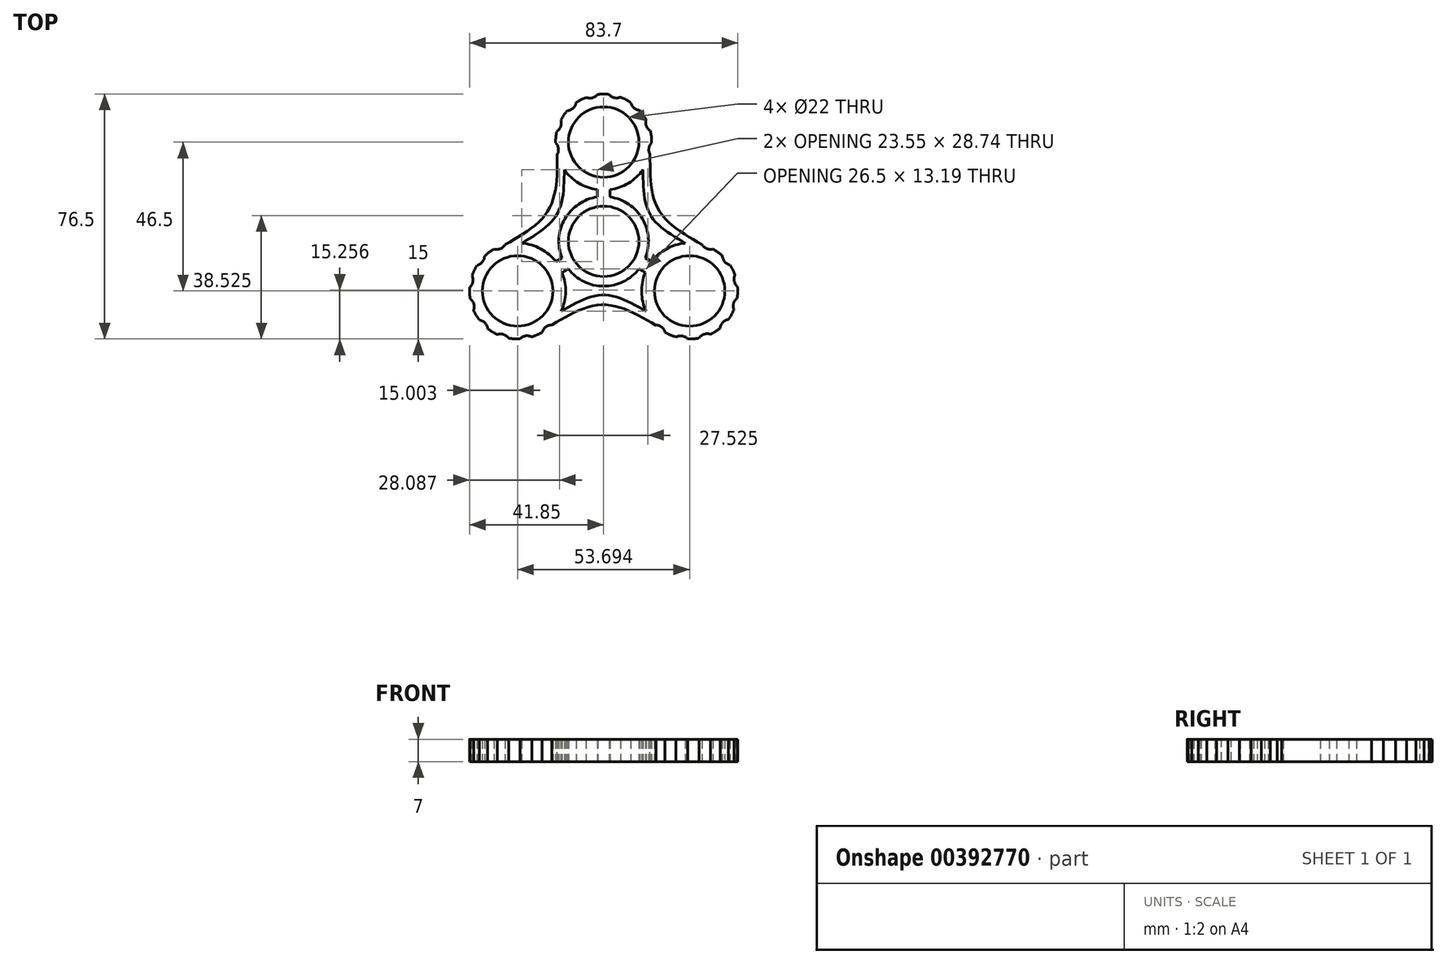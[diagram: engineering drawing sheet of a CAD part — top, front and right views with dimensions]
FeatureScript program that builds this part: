
annotation { "Feature Type Name" : "Feature", "Feature Type Description" : "" }
export const myFeature = defineFeature(function(context is Context, id is Id, definition is map)
    precondition{}
    {
        {
            var Q0;
            Q0=qCreatedBy(makeId("Top.planeOp"),FACE);
            var sketch = newSketch(context, id + "F0", { "sketchPlane" : qUnion([Q0])});
            skCircle(sketch, "E0", {"center": v(0, 0) * mm, "radius": 11 * mm});
            skCircle(sketch, "E1", {"center": v(0, 31) * mm, "radius": 11 * mm});
            skCircle(sketch, "E2.0", {"center": v(0, 0) * mm, "radius": 14 * mm});
            skArc(sketch, "E3.0", {"start": v(-14.49, 27.12) * mm, "mid": v(0.1, 16) * mm, "end": v(14.54, 27.3) * mm});
            skLineSegment(sketch, "E4", {"start": v(-1.99, 16.13) * mm, "end": v(-1.99, 13.86) * mm});
            skLineSegment(sketch, "E5.MirrorCS", {"start": v(1.99, 16.13) * mm, "end": v(1.99, 13.86) * mm});
            skLineSegment(sketch, "E6", {"start": v(0, 0) * mm, "end": v(-12.12, 7) * mm});
            skLineSegment(sketch, "E7", {"start": v(0, 31) * mm, "end": v(-14.49, 27.12) * mm, "construction": true});
            skLineSegment(sketch, "E8.MirrorCS", {"start": v(0, 31) * mm, "end": v(14.49, 27.12) * mm, "construction": true});
            skLineSegment(sketch, "E9", {"start": v(0, 31) * mm, "end": v(-12.29, 22.4) * mm, "construction": true});
            skLineSegment(sketch, "E10.MirrorCS", {"start": v(0, 31) * mm, "end": v(12.29, 22.4) * mm, "construction": true});
            skPoint(sketch, "E11.center", {"position": v(-1.16, -1.95) * mm});
            skPoint(sketch, "E12", {"position": v(-14.5, 8.41) * mm});
            skPoint(sketch, "E13.2.1", {"position": v(14.62, 8.4) * mm});
            skPoint(sketch, "E14.center", {"position": v(0, 0.05) * mm});
            skPoint(sketch, "E15", {"position": v(-17.14, 9.94) * mm});
            skPoint(sketch, "E16.MirrorP", {"position": v(17.14, 9.94) * mm});
            skArc(sketch, "E17", {"start": v(-14.49, 27.12) * mm, "mid": v(-14.12, 29.05) * mm, "end": v(-15, 30.8) * mm});
            skArc(sketch, "E18.MirrorCS", {"start": v(14.49, 27.12) * mm, "mid": v(14.12, 29.05) * mm, "end": v(15, 30.8) * mm});
            skPoint(sketch, "E19", {"position": v(14.49, 27.12) * mm});
            skPoint(sketch, "E20", {"position": v(15, 30.8) * mm});
            skArc(sketch, "E21.1.0", {"start": v(-14.62, 34.34) * mm, "mid": v(-13.4, 35.87) * mm, "end": v(-13.35, 37.83) * mm});
            skArc(sketch, "E21.2.0", {"start": v(-11.37, 40.78) * mm, "mid": v(-9.57, 41.56) * mm, "end": v(-8.61, 43.28) * mm});
            skArc(sketch, "E21.3.0", {"start": v(-5.48, 44.96) * mm, "mid": v(-3.52, 44.8) * mm, "end": v(-1.88, 45.88) * mm});
            skArc(sketch, "E21.4.0", {"start": v(1.68, 45.9) * mm, "mid": v(3.34, 44.85) * mm, "end": v(5.3, 45.03) * mm});
            skArc(sketch, "E21.5.0", {"start": v(8.45, 43.4) * mm, "mid": v(9.43, 41.69) * mm, "end": v(11.24, 40.93) * mm});
            skArc(sketch, "E21.6.0", {"start": v(13.26, 38) * mm, "mid": v(13.33, 36.05) * mm, "end": v(14.58, 34.53) * mm});
            skArc(sketch, "E21.7.0", {"start": v(14.14, 29.23) * mm, "mid": v(14.18, 28.24) * mm, "end": v(14.54, 27.3) * mm});
            skLineSegment(sketch, "E21.anchor1", {"start": v(0, 31) * mm, "end": v(-17.13, 28.63) * mm, "construction": true});
            skLineSegment(sketch, "E21.anchor2", {"start": v(0, 31) * mm, "end": v(17.16, 28.86) * mm, "construction": true});
            skArc(sketch, "E22.trimOffspring", {"start": v(-14.62, 34.34) * mm, "mid": v(-14.92, 32.58) * mm, "end": v(-15, 30.8) * mm});
            skArc(sketch, "E23.trimOffspring", {"start": v(-11.37, 40.78) * mm, "mid": v(-12.45, 39.37) * mm, "end": v(-13.35, 37.83) * mm});
            skArc(sketch, "E24.trimOffspring", {"start": v(-5.48, 44.96) * mm, "mid": v(-7.1, 44.22) * mm, "end": v(-8.61, 43.28) * mm});
            skArc(sketch, "E25.trimOffspring", {"start": v(1.68, 45.9) * mm, "mid": v(-0.1, 46) * mm, "end": v(-1.88, 45.88) * mm});
            skArc(sketch, "E26.trimOffspring", {"start": v(8.45, 43.4) * mm, "mid": v(6.92, 44.3) * mm, "end": v(5.3, 45.03) * mm});
            skArc(sketch, "E27.trimOffspring", {"start": v(13.26, 38) * mm, "mid": v(12.34, 39.53) * mm, "end": v(11.24, 40.93) * mm});
            skArc(sketch, "E28.trimOffspring", {"start": v(15, 30.8) * mm, "mid": v(14.9, 32.68) * mm, "end": v(14.58, 34.53) * mm});
            skPoint(sketch, "E29.orphan", {"position": v(15, 31) * mm});
            skArc(sketch, "E30.1.0", {"start": v(-40.6, -21.5) * mm, "mid": v(-39.79, -23.09) * mm, "end": v(-38.8, -24.57) * mm});
            skArc(sketch, "E30.1.1", {"start": v(-40.6, -21.5) * mm, "mid": v(-40.51, -19.54) * mm, "end": v(-41.65, -17.93) * mm});
            skArc(sketch, "E30.1.2", {"start": v(-41.8, -14.38) * mm, "mid": v(-41.83, -16.16) * mm, "end": v(-41.65, -17.93) * mm});
            skArc(sketch, "E30.1.3", {"start": v(-41.8, -14.38) * mm, "mid": v(-40.82, -12.68) * mm, "end": v(-41.07, -10.73) * mm});
            skArc(sketch, "E30.1.4", {"start": v(-39.55, -7.52) * mm, "mid": v(-40.4, -9.08) * mm, "end": v(-41.07, -10.73) * mm});
            skArc(sketch, "E30.1.5", {"start": v(-39.55, -7.52) * mm, "mid": v(-37.88, -6.48) * mm, "end": v(-37.2, -4.64) * mm});
            skPoint(sketch, "E30.1.6", {"position": v(-34.17, -2.41) * mm});
            skArc(sketch, "E30.1.7", {"start": v(-30.73, -1.01) * mm, "mid": v(-32.21, -2.3) * mm, "end": v(-34.17, -2.41) * mm});
            skArc(sketch, "E30.1.8", {"start": v(-34.17, -2.41) * mm, "mid": v(-35.75, -3.43) * mm, "end": v(-37.2, -4.64) * mm});
            skArc(sketch, "E30.1.9", {"start": v(-16.24, -26.1) * mm, "mid": v(-13.9, -7.91) * mm, "end": v(-30.92, -1.06) * mm});
            skArc(sketch, "E30.1.10", {"start": v(-16.24, -26.1) * mm, "mid": v(-18.1, -26.75) * mm, "end": v(-19.18, -28.4) * mm});
            skArc(sketch, "E30.1.11", {"start": v(-22.43, -29.83) * mm, "mid": v(-20.76, -29.2) * mm, "end": v(-19.18, -28.4) * mm});
            skArc(sketch, "E30.1.12", {"start": v(-22.43, -29.83) * mm, "mid": v(-24.37, -29.53) * mm, "end": v(-26.09, -30.48) * mm});
            skArc(sketch, "E30.1.13", {"start": v(-29.64, -30.24) * mm, "mid": v(-27.87, -30.47) * mm, "end": v(-26.09, -30.48) * mm});
            skArc(sketch, "E30.1.14", {"start": v(-29.64, -30.24) * mm, "mid": v(-31.21, -29.07) * mm, "end": v(-33.18, -29.1) * mm});
            skArc(sketch, "E30.1.15", {"start": v(-36.2, -27.23) * mm, "mid": v(-34.74, -28.25) * mm, "end": v(-33.18, -29.1) * mm});
            skArc(sketch, "E30.1.16", {"start": v(-36.2, -27.23) * mm, "mid": v(-37.04, -25.45) * mm, "end": v(-38.8, -24.57) * mm});
            skCircle(sketch, "E30.1.17", {"center": v(-26.85, -15.5) * mm, "radius": 11 * mm});
            skLineSegment(sketch, "E30.1.18", {"start": v(-14.96, -6.35) * mm, "end": v(-13, -5.2) * mm});
            skLineSegment(sketch, "E30.1.19", {"start": v(-12.98, -9.79) * mm, "end": v(-11, -8.65) * mm});
            skPoint(sketch, "E30.1.20", {"position": v(-0.04, -19.8) * mm});
            skPoint(sketch, "E30.1.21", {"position": v(-0.04, -16.76) * mm});
            skPoint(sketch, "E30.1.22", {"position": v(-14.58, 8.46) * mm});
            skPoint(sketch, "E30.1.23", {"position": v(-17.17, 9.87) * mm});
            skArc(sketch, "E30.2.0", {"start": v(38.92, -24.4) * mm, "mid": v(39.89, -22.91) * mm, "end": v(40.67, -21.32) * mm});
            skArc(sketch, "E30.2.1", {"start": v(38.92, -24.4) * mm, "mid": v(37.18, -25.32) * mm, "end": v(36.35, -27.1) * mm});
            skArc(sketch, "E30.2.2", {"start": v(33.36, -29.01) * mm, "mid": v(34.91, -28.15) * mm, "end": v(36.35, -27.1) * mm});
            skArc(sketch, "E30.2.3", {"start": v(33.36, -29.01) * mm, "mid": v(31.4, -29) * mm, "end": v(29.83, -30.2) * mm});
            skArc(sketch, "E30.2.4", {"start": v(26.29, -30.49) * mm, "mid": v(28.07, -30.45) * mm, "end": v(29.83, -30.2) * mm});
            skArc(sketch, "E30.2.5", {"start": v(26.29, -30.49) * mm, "mid": v(24.55, -29.56) * mm, "end": v(22.62, -29.9) * mm});
            skPoint(sketch, "E30.2.6", {"position": v(19.18, -28.4) * mm});
            skArc(sketch, "E30.2.7", {"start": v(16.24, -26.1) * mm, "mid": v(18.1, -26.75) * mm, "end": v(19.18, -28.4) * mm});
            skArc(sketch, "E30.2.8", {"start": v(19.18, -28.4) * mm, "mid": v(20.85, -29.25) * mm, "end": v(22.62, -29.9) * mm});
            skArc(sketch, "E30.2.9", {"start": v(30.73, -1.01) * mm, "mid": v(13.8, -8.09) * mm, "end": v(16.38, -26.25) * mm});
            skArc(sketch, "E30.2.10", {"start": v(30.73, -1.01) * mm, "mid": v(32.21, -2.3) * mm, "end": v(34.17, -2.41) * mm});
            skArc(sketch, "E30.2.11", {"start": v(37.05, -4.5) * mm, "mid": v(35.67, -3.37) * mm, "end": v(34.17, -2.41) * mm});
            skArc(sketch, "E30.2.12", {"start": v(37.05, -4.5) * mm, "mid": v(37.76, -6.34) * mm, "end": v(39.44, -7.35) * mm});
            skArc(sketch, "E30.2.13", {"start": v(41, -10.55) * mm, "mid": v(40.32, -8.9) * mm, "end": v(39.44, -7.35) * mm});
            skArc(sketch, "E30.2.14", {"start": v(41, -10.55) * mm, "mid": v(40.78, -12.5) * mm, "end": v(41.79, -14.18) * mm});
            skArc(sketch, "E30.2.15", {"start": v(41.68, -17.74) * mm, "mid": v(41.84, -15.96) * mm, "end": v(41.79, -14.18) * mm});
            skArc(sketch, "E30.2.16", {"start": v(41.68, -17.74) * mm, "mid": v(40.57, -19.35) * mm, "end": v(40.67, -21.32) * mm});
            skCircle(sketch, "E30.2.17", {"center": v(26.85, -15.5) * mm, "radius": 11 * mm});
            skLineSegment(sketch, "E30.2.18", {"start": v(12.98, -9.79) * mm, "end": v(11, -8.65) * mm});
            skLineSegment(sketch, "E30.2.19", {"start": v(14.96, -6.35) * mm, "end": v(13, -5.2) * mm});
            skPoint(sketch, "E30.2.20", {"position": v(17.17, 9.87) * mm});
            skPoint(sketch, "E30.2.21", {"position": v(14.53, 8.35) * mm});
            skPoint(sketch, "E30.2.22", {"position": v(-0.04, -16.86) * mm});
            skPoint(sketch, "E30.2.23", {"position": v(0.04, -19.8) * mm});
            skLineSegment(sketch, "E31.1.0", {"start": v(-26.85, -15.5) * mm, "end": v(-13.25, -21.84) * mm, "construction": true});
            skLineSegment(sketch, "E31.1.1", {"start": v(-26.85, -15.5) * mm, "end": v(-16.24, -26.1) * mm, "construction": true});
            skLineSegment(sketch, "E31.1.2", {"start": v(-26.85, -15.5) * mm, "end": v(-25.54, -0.56) * mm, "construction": true});
            skLineSegment(sketch, "E31.1.3", {"start": v(-26.85, -15.5) * mm, "end": v(-30.73, -1.01) * mm, "construction": true});
            skLineSegment(sketch, "E31.2.0", {"start": v(26.85, -15.5) * mm, "end": v(25.54, -0.56) * mm, "construction": true});
            skLineSegment(sketch, "E31.2.1", {"start": v(26.85, -15.5) * mm, "end": v(30.73, -1.01) * mm, "construction": true});
            skLineSegment(sketch, "E31.2.2", {"start": v(26.85, -15.5) * mm, "end": v(13.25, -21.84) * mm, "construction": true});
            skLineSegment(sketch, "E31.2.3", {"start": v(26.85, -15.5) * mm, "end": v(16.24, -26.1) * mm, "construction": true});
            skFitSpline(sketch, "E32", {"points": [v(12.29, 22.4) * mm, v(14.53, 8.35) * mm, v(25.54, -0.56) * mm], "startDerivative": vector(0.1, -30.62) * mm, "endDerivative": vector(26.42, -15.28) * mm});
            skFitSpline(sketch, "E33", {"points": [v(14.49, 27.12) * mm, v(17.17, 9.87) * mm, v(30.73, -1.01) * mm], "startDerivative": vector(-0.08, -37.62) * mm, "endDerivative": vector(32.58, -18.63) * mm});
            skFitSpline(sketch, "E34", {"points": [v(16.38, -26.25) * mm, v(0.04, -19.8) * mm, v(-16.24, -26.1) * mm], "startDerivative": vector(-32.65, 19.23) * mm, "endDerivative": vector(-32.6, -18.97) * mm});
            skFitSpline(sketch, "E35", {"points": [v(-13.25, -21.84) * mm, v(-0.04, -16.76) * mm, v(13.25, -21.84) * mm], "startDerivative": vector(26.44, 15.24) * mm, "endDerivative": vector(26.56, -15.23) * mm});
            skFitSpline(sketch, "E36", {"points": [v(-30.73, -1.01) * mm, v(-17.14, 9.94) * mm, v(-14.49, 27.12) * mm], "startDerivative": vector(32.62, 18.74) * mm, "endDerivative": vector(-0.15, 37.53) * mm});
            skFitSpline(sketch, "E37", {"points": [v(-12.29, 22.4) * mm, v(-14.58, 8.46) * mm, v(-25.54, -0.56) * mm], "startDerivative": vector(-0.28, -30.37) * mm, "endDerivative": vector(-26.21, -15.54) * mm});
            skSolve(sketch);
        }
        {
            var Q0;
            Q0=makeQuery(id+"F0.imprint","IMPRINT",FACE,{"disambiguationData":[TD([[makeQuery(id+"F0.imprint","IMPRINT",EDGE,{"derivedFrom":sQuery(id+"F0.wireOp",EDGE,"E1")}),-1.0]])]});
            var Q1;
            {var subQ0=sQuery(id+"F0.wireOp",EDGE,"E4");Q1=makeQuery(id+"F0.imprint","IMPRINT",FACE,{"disambiguationData":[TD([[makeQuery(id+"F0.imprint","IMPRINT",EDGE,{"derivedFrom":subQ0}),1.0]])]});}
            var Q2;
            {var subQ0=sQuery(id+"F0.wireOp",EDGE,"E30.2.18");Q2=makeQuery(id+"F0.imprint","IMPRINT",FACE,{"disambiguationData":[TD([[makeQuery(id+"F0.imprint","IMPRINT",EDGE,{"derivedFrom":subQ0}),-1.0]])]});}
            var Q3;
            {var subQ0=sQuery(id+"F0.wireOp",EDGE,"E30.1.18");Q3=makeQuery(id+"F0.imprint","IMPRINT",FACE,{"disambiguationData":[TD([[makeQuery(id+"F0.imprint","IMPRINT",EDGE,{"derivedFrom":subQ0}),-1.0]])]});}
            var Q4;
            Q4=makeQuery(id+"F0.imprint","IMPRINT",FACE,{"disambiguationData":[TD([[makeQuery(id+"F0.imprint","IMPRINT",EDGE,{"derivedFrom":sQuery(id+"F0.wireOp",EDGE,"E0")}),-1.0]])]});
            var Q5;
            {var subQ0=sQuery(id+"F0.wireOp",EDGE,"E36");Q5=makeQuery(id+"F0.imprint","IMPRINT",FACE,{"disambiguationData":[TD([[makeQuery(id+"F0.imprint","IMPRINT",EDGE,{"derivedFrom":subQ0}),-1.0]])]});}
            var Q6;
            {var subQ2=sQuery(id+"F0.wireOp",EDGE,"E32");Q6=makeQuery(id+"F0.imprint","IMPRINT",FACE,{"disambiguationData":[TD([[makeQuery(id+"F0.imprint","IMPRINT",EDGE,{"derivedFrom":subQ2}),1.0]])]});}
            var Q7;
            Q7=makeQuery(id+"F0.imprint","IMPRINT",FACE,{"disambiguationData":[TD([[makeQuery(id+"F0.imprint","IMPRINT",EDGE,{"derivedFrom":sQuery(id+"F0.wireOp",EDGE,"E30.2.0")}),1.0]])]});
            var Q8;
            {var subQ0=sQuery(id+"F0.wireOp",EDGE,"E34");Q8=makeQuery(id+"F0.imprint","IMPRINT",FACE,{"disambiguationData":[TD([[makeQuery(id+"F0.imprint","IMPRINT",EDGE,{"derivedFrom":subQ0}),-1.0]])]});}
            var Q9;
            Q9=makeQuery(id+"F0.imprint","IMPRINT",FACE,{"disambiguationData":[TD([[makeQuery(id+"F0.imprint","IMPRINT",EDGE,{"derivedFrom":sQuery(id+"F0.wireOp",EDGE,"E30.1.0")}),1.0]])]});
            extrude(context, id + "F1", {"entities" : qUnion([Q0, Q1, Q2, Q3, Q4, Q5, Q6, Q7, Q8, Q9]), "endBound" : BoundingType.SYMMETRIC, "depth" : 7 * mm});
        }
    });
